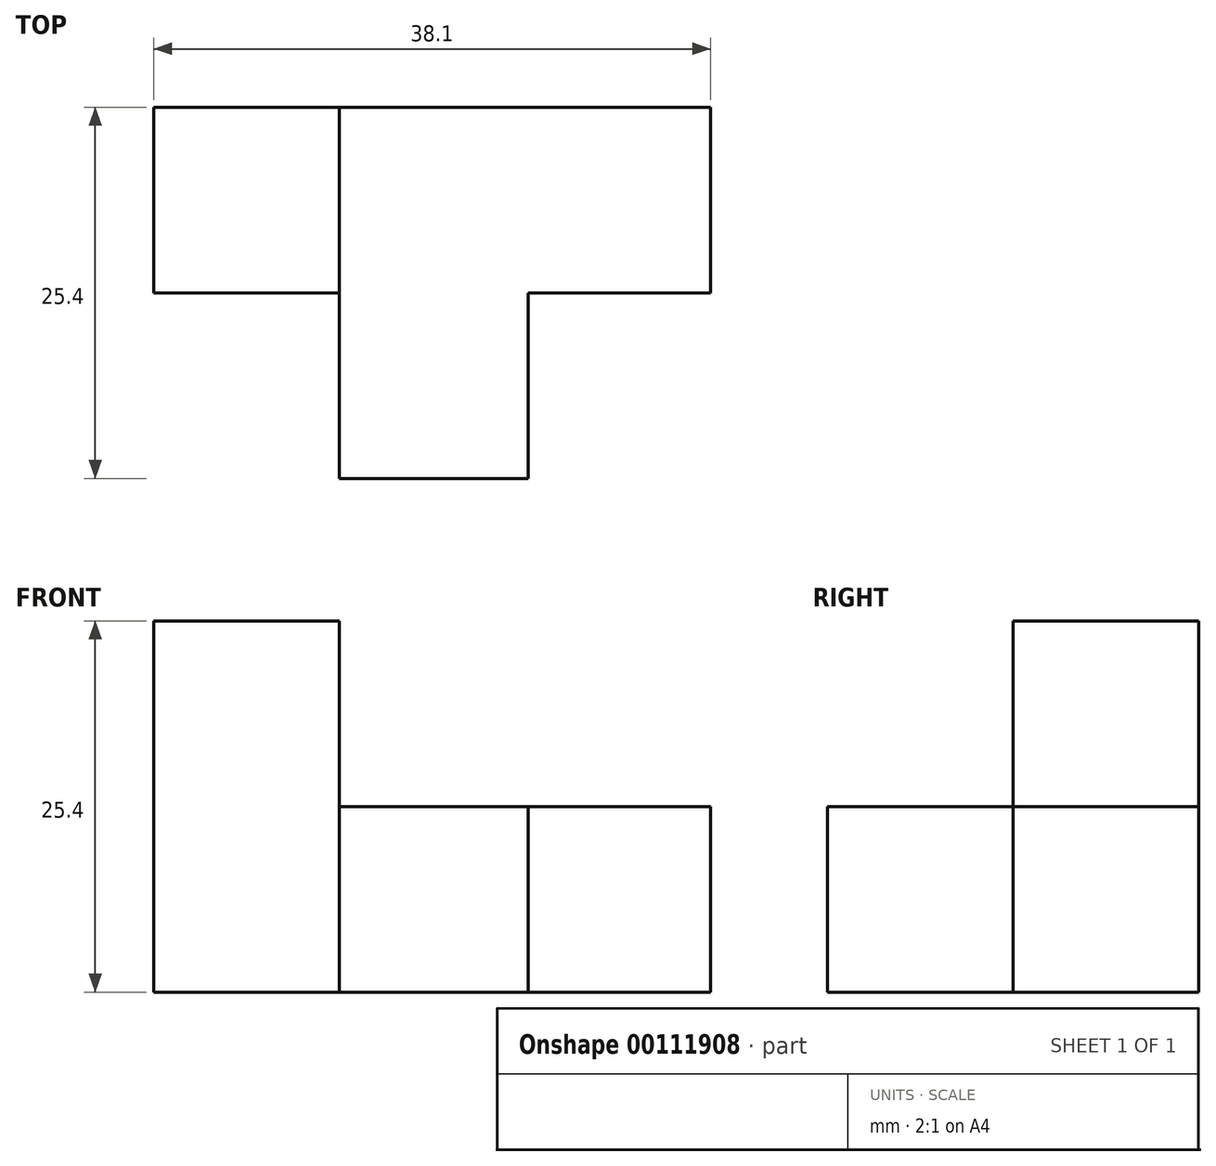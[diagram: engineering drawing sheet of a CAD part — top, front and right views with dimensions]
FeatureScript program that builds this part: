
annotation { "Feature Type Name" : "Feature", "Feature Type Description" : "" }
export const myFeature = defineFeature(function(context is Context, id is Id, definition is map)
    precondition{}
    {
        {
            var Q0;
            Q0=qCreatedBy(makeId("Front.planeOp"),FACE);
            var sketch = newSketch(context, id + "F0", { "sketchPlane" : qUnion([Q0])});
            skLineSegment(sketch, "E0.bottom", {"start": v(-18.5, 8.17) * mm, "end": v(19.6, 8.17) * mm});
            skLineSegment(sketch, "E0.top", {"start": v(-18.5, -4.53) * mm, "end": v(19.6, -4.53) * mm});
            skLineSegment(sketch, "E0.left", {"start": v(-18.5, 8.17) * mm, "end": v(-18.5, -4.53) * mm});
            skLineSegment(sketch, "E0.right", {"start": v(19.6, 8.17) * mm, "end": v(19.6, -4.53) * mm});
            skSolve(sketch);
        }
        {
            var Q0;
            Q0=makeQuery(id+"F0.imprint","IMPRINT",FACE,{"disambiguationData":[TD([[makeQuery(id+"F0.imprint","IMPRINT",EDGE,{"derivedFrom":sQuery(id+"F0.wireOp",EDGE,"E0.bottom")}),-1.0]])]});
            extrude(context, id + "F1", {"entities" : qUnion([Q0]), "depth" : 12.7 * mm});
        }
        {
            var Q0;
            Q0=makeQuery(id+"F1.opExtrude","CAP_FACE",FACE,{"disambiguationData":[OSD([sQuery(id+"F0.wireOp",EDGE,"E0.bottom"),sQuery(id+"F0.wireOp",EDGE,"E0.top"),sQuery(id+"F0.wireOp",EDGE,"E0.left"),sQuery(id+"F0.wireOp",EDGE,"E0.right")])],"isStart":false});
            var sketch = newSketch(context, id + "F2", { "sketchPlane" : qUnion([Q0])});
            skLineSegment(sketch, "E1", {"start": v(-18.5, -4.53) * mm, "end": v(-5.8, -4.53) * mm});
            skLineSegment(sketch, "E2", {"start": v(-5.8, -4.53) * mm, "end": v(7.13, -4.53) * mm});
            skLineSegment(sketch, "E3", {"start": v(-5.8, -4.53) * mm, "end": v(-5.8, 8.17) * mm});
            skLineSegment(sketch, "E4", {"start": v(7.13, -4.53) * mm, "end": v(7.13, 8.17) * mm});
            skSolve(sketch);
        }
        {
            var Q0;
            Q0 = qSketchRegion(id + "F2", true);
            var Q1;
            Q1=makeQuery(id+"F2.imprint","IMPRINT",FACE,{"disambiguationData":[TD([[makeQuery(id+"F2.imprint","IMPRINT",EDGE,{"derivedFrom":sQuery(id+"F2.wireOp",EDGE,"E2")}),1.0]])]});
            extrude(context, id + "F3", {"entities" : qUnion([Q0, Q1]), "operationType" : NewBodyOperationType.ADD, "depth" : 12.7 * mm});
        }
        {
            var Q0;
            {var subQ0=sQuery(id+"F0.wireOp",EDGE,"E0.bottom");Q0=makeQuery(id+"F3.boolean.opBoolean","MERGE",FACE,{"derivedFrom":[makeQuery(id+"F1.opExtrude","SWEPT_FACE",FACE,{"disambiguationData":[OSD([subQ0])]}),makeQuery(id+"F3.opExtrude","SWEPT_FACE",FACE,{"disambiguationData":[OSD([subQ0])]})]});}
            var sketch = newSketch(context, id + "F4", { "sketchPlane" : qUnion([Q0])});
            skLineSegment(sketch, "E5", {"start": v(-5.8, -12.7) * mm, "end": v(-5.8, 0) * mm});
            skSolve(sketch);
        }
        {
            var Q0;
            Q0 = qSketchRegion(id + "F4", true);
            var Q1;
            {var subQ0=sQuery(id+"F4.wireOp",EDGE,"E5");Q1=makeQuery(id+"F4.imprint","IMPRINT",FACE,{"disambiguationData":[TD([[makeQuery(id+"F4.imprint","IMPRINT",EDGE,{"derivedFrom":subQ0}),1.0]])]});}
            extrude(context, id + "F5", {"entities" : qUnion([Q0, Q1]), "operationType" : NewBodyOperationType.ADD, "depth" : 12.7 * mm});
        }
    });
